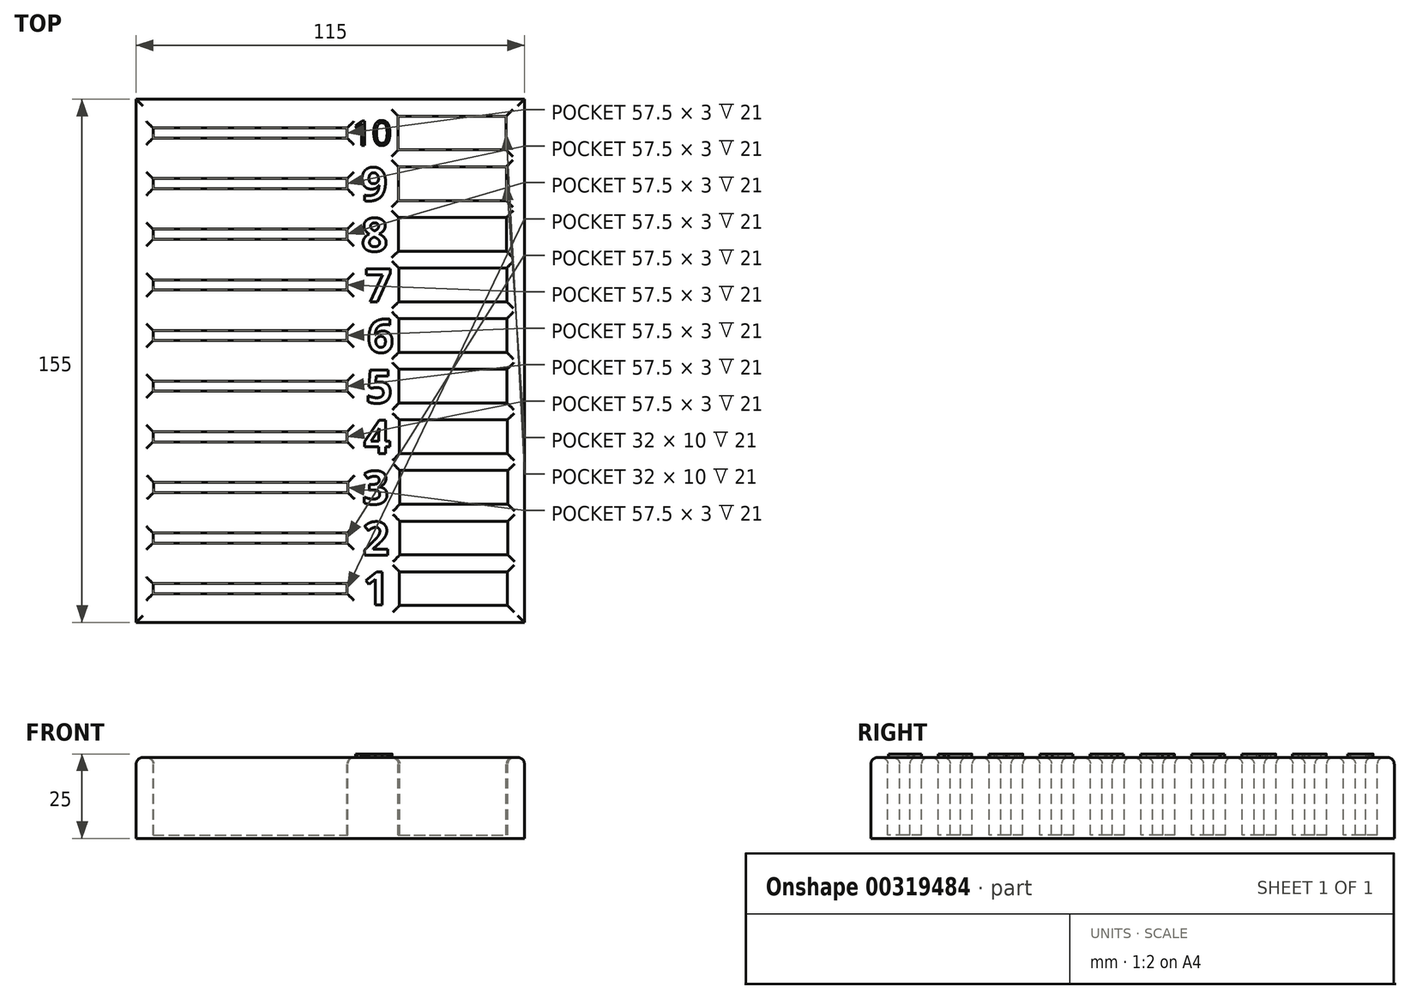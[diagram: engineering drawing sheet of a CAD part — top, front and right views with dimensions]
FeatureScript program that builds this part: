
annotation { "Feature Type Name" : "Feature", "Feature Type Description" : "" }
export const myFeature = defineFeature(function(context is Context, id is Id, definition is map)
    precondition{}
    {
        {
            var Q0;
            Q0=qCreatedBy(makeId("Top.planeOp"),FACE);
            var sketch = newSketch(context, id + "F0", { "sketchPlane" : qUnion([Q0])});
            skLineSegment(sketch, "E0.bottom", {"start": v(-49.85, 126.63) * mm, "end": v(65.15, 126.63) * mm});
            skLineSegment(sketch, "E0.top", {"start": v(-49.85, -28.37) * mm, "end": v(65.15, -28.37) * mm});
            skLineSegment(sketch, "E0.left", {"start": v(-49.85, 126.63) * mm, "end": v(-49.85, -28.37) * mm});
            skLineSegment(sketch, "E0.right", {"start": v(65.15, 126.63) * mm, "end": v(65.15, -28.37) * mm});
            skSolve(sketch);
        }
        {
            var Q0;
            Q0=makeQuery(id+"F0.imprint","IMPRINT",FACE,{"disambiguationData":[TD([[makeQuery(id+"F0.imprint","IMPRINT",EDGE,{"derivedFrom":sQuery(id+"F0.wireOp",EDGE,"E0.bottom")}),-1.0]])]});
            var Q1;
            Q1=makeQuery(id+"F0.imprint","IMPRINT",FACE,{"disambiguationData":[TD([[makeQuery(id+"F0.imprint","IMPRINT",EDGE,{"derivedFrom":sQuery(id+"F0.wireOp",EDGE,"eXpO4zti-W6eb-gkUP-Bc0d-zbJJjk6ygzeg.bottom")}),-1.0]])]});
            var Q2;
            Q2=makeQuery(id+"F0.imprint","IMPRINT",FACE,{"disambiguationData":[TD([[makeQuery(id+"F0.imprint","IMPRINT",EDGE,{"derivedFrom":sQuery(id+"F0.wireOp",EDGE,"IiJkesfC-iyIp-GpGT-9vFS-BzQ84R5pHUzr.bottom")}),-1.0]])]});
            extrude(context, id + "F1", {"entities" : qUnion([Q0, Q1, Q2]), "depth" : 24 * mm});
        }
        {
            var Q0;
            Q0=makeQuery(id+"F1.opExtrude","CAP_FACE",FACE,{"disambiguationData":[OSD([sQuery(id+"F0.wireOp",EDGE,"E0.bottom"),sQuery(id+"F0.wireOp",EDGE,"E0.top"),sQuery(id+"F0.wireOp",EDGE,"E0.left"),sQuery(id+"F0.wireOp",EDGE,"E0.right")])],"isStart":false});
            var sketch = newSketch(context, id + "F2", { "sketchPlane" : qUnion([Q0])});
            skLineSegment(sketch, "E1.bottom", {"start": v(-44.85, -16.87) * mm, "end": v(12.65, -16.87) * mm});
            skLineSegment(sketch, "E1.top", {"start": v(-44.85, -19.87) * mm, "end": v(12.65, -19.87) * mm});
            skLineSegment(sketch, "E1.left", {"start": v(-44.85, -16.87) * mm, "end": v(-44.85, -19.87) * mm});
            skLineSegment(sketch, "E1.right", {"start": v(12.65, -16.87) * mm, "end": v(12.65, -19.87) * mm});
            skLineSegment(sketch, "E2.bottom", {"start": v(28.15, -13.37) * mm, "end": v(60.15, -13.37) * mm});
            skLineSegment(sketch, "E2.top", {"start": v(28.15, -23.37) * mm, "end": v(60.15, -23.37) * mm});
            skLineSegment(sketch, "E2.left", {"start": v(28.15, -13.37) * mm, "end": v(28.15, -23.37) * mm});
            skLineSegment(sketch, "E2.right", {"start": v(60.15, -13.37) * mm, "end": v(60.15, -23.37) * mm});
            skText(sketch, "E3", { "text": "1", "fontName": "OpenSans-Bold.ttf"});
            skLineSegment(sketch, "E4.bottom", {"start": v(-44.87, -1.87) * mm, "end": v(12.63, -1.87) * mm});
            skLineSegment(sketch, "E4.top", {"start": v(-44.87, -4.87) * mm, "end": v(12.63, -4.87) * mm});
            skLineSegment(sketch, "E4.left", {"start": v(-44.87, -1.87) * mm, "end": v(-44.87, -4.87) * mm});
            skLineSegment(sketch, "E4.right", {"start": v(12.63, -1.87) * mm, "end": v(12.63, -4.87) * mm});
            skLineSegment(sketch, "E5.bottom", {"start": v(28.23, 1.63) * mm, "end": v(60.23, 1.63) * mm});
            skLineSegment(sketch, "E5.top", {"start": v(28.23, -8.37) * mm, "end": v(60.23, -8.37) * mm});
            skLineSegment(sketch, "E5.left", {"start": v(28.23, 1.63) * mm, "end": v(28.23, -8.37) * mm});
            skLineSegment(sketch, "E5.right", {"start": v(60.23, 1.63) * mm, "end": v(60.23, -8.37) * mm});
            skLineSegment(sketch, "E6.bottom", {"start": v(28.24, 16.63) * mm, "end": v(60.24, 16.63) * mm});
            skLineSegment(sketch, "E6.top", {"start": v(28.24, 6.63) * mm, "end": v(60.24, 6.63) * mm});
            skLineSegment(sketch, "E6.left", {"start": v(28.24, 16.63) * mm, "end": v(28.24, 6.63) * mm});
            skLineSegment(sketch, "E6.right", {"start": v(60.24, 16.63) * mm, "end": v(60.24, 6.63) * mm});
            skLineSegment(sketch, "E7.bottom", {"start": v(28.1, 31.63) * mm, "end": v(60.1, 31.63) * mm});
            skLineSegment(sketch, "E7.top", {"start": v(28.1, 21.63) * mm, "end": v(60.1, 21.63) * mm});
            skLineSegment(sketch, "E7.left", {"start": v(28.1, 31.63) * mm, "end": v(28.1, 21.63) * mm});
            skLineSegment(sketch, "E7.right", {"start": v(60.1, 31.63) * mm, "end": v(60.1, 21.63) * mm});
            skLineSegment(sketch, "E8.bottom", {"start": v(28, 46.63) * mm, "end": v(60, 46.63) * mm});
            skLineSegment(sketch, "E8.top", {"start": v(28, 36.63) * mm, "end": v(60, 36.63) * mm});
            skLineSegment(sketch, "E8.left", {"start": v(28, 46.63) * mm, "end": v(28, 36.63) * mm});
            skLineSegment(sketch, "E8.right", {"start": v(60, 46.63) * mm, "end": v(60, 36.63) * mm});
            skLineSegment(sketch, "E9.bottom", {"start": v(27.93, 61.63) * mm, "end": v(59.93, 61.63) * mm});
            skLineSegment(sketch, "E9.top", {"start": v(27.93, 51.63) * mm, "end": v(59.93, 51.63) * mm});
            skLineSegment(sketch, "E9.left", {"start": v(27.93, 61.63) * mm, "end": v(27.93, 51.63) * mm});
            skLineSegment(sketch, "E9.right", {"start": v(59.93, 61.63) * mm, "end": v(59.93, 51.63) * mm});
            skLineSegment(sketch, "E10.bottom", {"start": v(27.91, 76.63) * mm, "end": v(59.91, 76.63) * mm});
            skLineSegment(sketch, "E10.top", {"start": v(27.91, 66.63) * mm, "end": v(59.91, 66.63) * mm});
            skLineSegment(sketch, "E10.left", {"start": v(27.91, 76.63) * mm, "end": v(27.91, 66.63) * mm});
            skLineSegment(sketch, "E10.right", {"start": v(59.91, 76.63) * mm, "end": v(59.91, 66.63) * mm});
            skLineSegment(sketch, "E11.bottom", {"start": v(27.82, 91.63) * mm, "end": v(59.82, 91.63) * mm});
            skLineSegment(sketch, "E11.top", {"start": v(27.82, 81.63) * mm, "end": v(59.82, 81.63) * mm});
            skLineSegment(sketch, "E11.left", {"start": v(27.82, 91.63) * mm, "end": v(27.82, 81.63) * mm});
            skLineSegment(sketch, "E11.right", {"start": v(59.82, 91.63) * mm, "end": v(59.82, 81.63) * mm});
            skLineSegment(sketch, "E12.bottom", {"start": v(27.78, 106.63) * mm, "end": v(59.78, 106.63) * mm});
            skLineSegment(sketch, "E12.top", {"start": v(27.78, 96.63) * mm, "end": v(59.78, 96.63) * mm});
            skLineSegment(sketch, "E12.left", {"start": v(27.78, 106.63) * mm, "end": v(27.78, 96.63) * mm});
            skLineSegment(sketch, "E12.right", {"start": v(59.78, 106.63) * mm, "end": v(59.78, 96.63) * mm});
            skLineSegment(sketch, "E13.bottom", {"start": v(27.76, 121.63) * mm, "end": v(59.76, 121.63) * mm});
            skLineSegment(sketch, "E13.top", {"start": v(27.76, 111.63) * mm, "end": v(59.76, 111.63) * mm});
            skLineSegment(sketch, "E13.left", {"start": v(27.76, 121.63) * mm, "end": v(27.76, 111.63) * mm});
            skLineSegment(sketch, "E13.right", {"start": v(59.76, 121.63) * mm, "end": v(59.76, 111.63) * mm});
            skLineSegment(sketch, "E14.bottom", {"start": v(-44.66, 13.13) * mm, "end": v(12.84, 13.13) * mm});
            skLineSegment(sketch, "E14.top", {"start": v(-44.66, 10.13) * mm, "end": v(12.84, 10.13) * mm});
            skLineSegment(sketch, "E14.left", {"start": v(-44.66, 13.13) * mm, "end": v(-44.66, 10.13) * mm});
            skLineSegment(sketch, "E14.right", {"start": v(12.84, 13.13) * mm, "end": v(12.84, 10.13) * mm});
            skLineSegment(sketch, "E15.bottom", {"start": v(-44.85, 28.13) * mm, "end": v(12.65, 28.13) * mm});
            skLineSegment(sketch, "E15.top", {"start": v(-44.85, 25.13) * mm, "end": v(12.65, 25.13) * mm});
            skLineSegment(sketch, "E15.left", {"start": v(-44.85, 28.13) * mm, "end": v(-44.85, 25.13) * mm});
            skLineSegment(sketch, "E15.right", {"start": v(12.65, 28.13) * mm, "end": v(12.65, 25.13) * mm});
            skLineSegment(sketch, "E16.bottom", {"start": v(-44.85, 43.13) * mm, "end": v(12.65, 43.13) * mm});
            skLineSegment(sketch, "E16.top", {"start": v(-44.85, 40.13) * mm, "end": v(12.65, 40.13) * mm});
            skLineSegment(sketch, "E16.left", {"start": v(-44.85, 43.13) * mm, "end": v(-44.85, 40.13) * mm});
            skLineSegment(sketch, "E16.right", {"start": v(12.65, 43.13) * mm, "end": v(12.65, 40.13) * mm});
            skLineSegment(sketch, "E17.bottom", {"start": v(-44.85, 58.13) * mm, "end": v(12.65, 58.13) * mm});
            skLineSegment(sketch, "E17.top", {"start": v(-44.85, 55.13) * mm, "end": v(12.65, 55.13) * mm});
            skLineSegment(sketch, "E17.left", {"start": v(-44.85, 58.13) * mm, "end": v(-44.85, 55.13) * mm});
            skLineSegment(sketch, "E17.right", {"start": v(12.65, 58.13) * mm, "end": v(12.65, 55.13) * mm});
            skLineSegment(sketch, "E18.bottom", {"start": v(-44.85, 73.13) * mm, "end": v(12.65, 73.13) * mm});
            skLineSegment(sketch, "E18.top", {"start": v(-44.85, 70.13) * mm, "end": v(12.65, 70.13) * mm});
            skLineSegment(sketch, "E18.left", {"start": v(-44.85, 73.13) * mm, "end": v(-44.85, 70.13) * mm});
            skLineSegment(sketch, "E18.right", {"start": v(12.65, 73.13) * mm, "end": v(12.65, 70.13) * mm});
            skLineSegment(sketch, "E19.bottom", {"start": v(-44.85, 88.13) * mm, "end": v(12.65, 88.13) * mm});
            skLineSegment(sketch, "E19.top", {"start": v(-44.85, 85.13) * mm, "end": v(12.65, 85.13) * mm});
            skLineSegment(sketch, "E19.left", {"start": v(-44.85, 88.13) * mm, "end": v(-44.85, 85.13) * mm});
            skLineSegment(sketch, "E19.right", {"start": v(12.65, 88.13) * mm, "end": v(12.65, 85.13) * mm});
            skLineSegment(sketch, "E20.bottom", {"start": v(-44.85, 103.13) * mm, "end": v(12.65, 103.13) * mm});
            skLineSegment(sketch, "E20.top", {"start": v(-44.85, 100.13) * mm, "end": v(12.65, 100.13) * mm});
            skLineSegment(sketch, "E20.left", {"start": v(-44.85, 103.13) * mm, "end": v(-44.85, 100.13) * mm});
            skLineSegment(sketch, "E20.right", {"start": v(12.65, 103.13) * mm, "end": v(12.65, 100.13) * mm});
            skLineSegment(sketch, "E21.bottom", {"start": v(-44.85, 118.13) * mm, "end": v(12.65, 118.13) * mm});
            skLineSegment(sketch, "E21.top", {"start": v(-44.85, 115.13) * mm, "end": v(12.65, 115.13) * mm});
            skLineSegment(sketch, "E21.left", {"start": v(-44.85, 118.13) * mm, "end": v(-44.85, 115.13) * mm});
            skLineSegment(sketch, "E21.right", {"start": v(12.65, 118.13) * mm, "end": v(12.65, 115.13) * mm});
            skText(sketch, "E22", { "text": "2", "fontName": "OpenSans-Bold.ttf"});
            skText(sketch, "E23", { "text": "3", "fontName": "OpenSans-Bold.ttf"});
            skText(sketch, "E24", { "text": "4", "fontName": "OpenSans-Bold.ttf"});
            skText(sketch, "E25", { "text": "5", "fontName": "OpenSans-Bold.ttf"});
            skText(sketch, "E26", { "text": "6", "fontName": "OpenSans-Bold.ttf"});
            skText(sketch, "E27", { "text": "7", "fontName": "OpenSans-Bold.ttf"});
            skText(sketch, "E28", { "text": "8", "fontName": "OpenSans-Bold.ttf"});
            skText(sketch, "E29", { "text": "9", "fontName": "OpenSans-Bold.ttf"});
            skText(sketch, "E30", { "text": "10", "fontName": "OpenSans-Regular.ttf"});
            const initialGuessF2  = {"E3": [0.01732, -0.0232, 1, 0, 0.0099], "E22": [0.01725, -0.00843, 1, 0, 0.0099], "E23": [0.01713, 0.00666, 1, 0, 0.0099], "E24": [0.01761, 0.02167, 1, 0, 0.0099], "E25": [0.01821, 0.03663, 1, 0, 0.0099], "E26": [0.01857, 0.0516, 1, 0, 0.0099], "E27": [0.01797, 0.0666, 1, 0, 0.0099], "E28": [0.01684, 0.08158, 1, 0, 0.0099], "E29": [0.01664, 0.0966, 1, 0, 0.0099], "E30": [0.0142, 0.113, 1, 0, 0.00732]};
            skSetInitialGuess(sketch, initialGuessF2);
            skSolve(sketch);
        }
        {
            var Q0;
            Q0=makeQuery(id+"F2.imprint","IMPRINT",FACE,{"disambiguationData":[TD([[makeQuery(id+"F2.imprint","IMPRINT",EDGE,{"derivedFrom":sQuery(id+"F2.wireOp",EDGE,"E2.bottom")}),-1.0]])]});
            var Q1;
            Q1=makeQuery(id+"F2.imprint","IMPRINT",FACE,{"disambiguationData":[TD([[makeQuery(id+"F2.imprint","IMPRINT",EDGE,{"derivedFrom":sQuery(id+"F2.wireOp",EDGE,"E1.bottom")}),-1.0]])]});
            var Q2;
            Q2=makeQuery(id+"F2.imprint","IMPRINT",FACE,{"disambiguationData":[TD([[makeQuery(id+"F2.imprint","IMPRINT",EDGE,{"derivedFrom":sQuery(id+"F2.wireOp",EDGE,"E4.bottom")}),-1.0]])]});
            var Q3;
            Q3=makeQuery(id+"F2.imprint","IMPRINT",FACE,{"disambiguationData":[TD([[makeQuery(id+"F2.imprint","IMPRINT",EDGE,{"derivedFrom":sQuery(id+"F2.wireOp",EDGE,"E5.bottom")}),-1.0]])]});
            var Q4;
            Q4=makeQuery(id+"F2.imprint","IMPRINT",FACE,{"disambiguationData":[TD([[makeQuery(id+"F2.imprint","IMPRINT",EDGE,{"derivedFrom":sQuery(id+"F2.wireOp",EDGE,"E6.bottom")}),-1.0]])]});
            var Q5;
            Q5=makeQuery(id+"F2.imprint","IMPRINT",FACE,{"disambiguationData":[TD([[makeQuery(id+"F2.imprint","IMPRINT",EDGE,{"derivedFrom":sQuery(id+"F2.wireOp",EDGE,"E7.bottom")}),-1.0]])]});
            var Q6;
            Q6=makeQuery(id+"F2.imprint","IMPRINT",FACE,{"disambiguationData":[TD([[makeQuery(id+"F2.imprint","IMPRINT",EDGE,{"derivedFrom":sQuery(id+"F2.wireOp",EDGE,"E8.bottom")}),-1.0]])]});
            var Q7;
            Q7=makeQuery(id+"F2.imprint","IMPRINT",FACE,{"disambiguationData":[TD([[makeQuery(id+"F2.imprint","IMPRINT",EDGE,{"derivedFrom":sQuery(id+"F2.wireOp",EDGE,"E9.bottom")}),-1.0]])]});
            var Q8;
            Q8=makeQuery(id+"F2.imprint","IMPRINT",FACE,{"disambiguationData":[TD([[makeQuery(id+"F2.imprint","IMPRINT",EDGE,{"derivedFrom":sQuery(id+"F2.wireOp",EDGE,"E10.bottom")}),-1.0]])]});
            var Q9;
            Q9=makeQuery(id+"F2.imprint","IMPRINT",FACE,{"disambiguationData":[TD([[makeQuery(id+"F2.imprint","IMPRINT",EDGE,{"derivedFrom":sQuery(id+"F2.wireOp",EDGE,"E11.bottom")}),-1.0]])]});
            var Q10;
            Q10=makeQuery(id+"F2.imprint","IMPRINT",FACE,{"disambiguationData":[TD([[makeQuery(id+"F2.imprint","IMPRINT",EDGE,{"derivedFrom":sQuery(id+"F2.wireOp",EDGE,"E12.bottom")}),-1.0]])]});
            var Q11;
            Q11=makeQuery(id+"F2.imprint","IMPRINT",FACE,{"disambiguationData":[TD([[makeQuery(id+"F2.imprint","IMPRINT",EDGE,{"derivedFrom":sQuery(id+"F2.wireOp",EDGE,"E13.bottom")}),-1.0]])]});
            var Q12;
            Q12=makeQuery(id+"F2.imprint","IMPRINT",FACE,{"disambiguationData":[TD([[makeQuery(id+"F2.imprint","IMPRINT",EDGE,{"derivedFrom":sQuery(id+"F2.wireOp",EDGE,"E14.bottom")}),-1.0]])]});
            var Q13;
            Q13=makeQuery(id+"F2.imprint","IMPRINT",FACE,{"disambiguationData":[TD([[makeQuery(id+"F2.imprint","IMPRINT",EDGE,{"derivedFrom":sQuery(id+"F2.wireOp",EDGE,"E15.bottom")}),-1.0]])]});
            var Q14;
            Q14=makeQuery(id+"F2.imprint","IMPRINT",FACE,{"disambiguationData":[TD([[makeQuery(id+"F2.imprint","IMPRINT",EDGE,{"derivedFrom":sQuery(id+"F2.wireOp",EDGE,"E16.bottom")}),-1.0]])]});
            var Q15;
            Q15=makeQuery(id+"F2.imprint","IMPRINT",FACE,{"disambiguationData":[TD([[makeQuery(id+"F2.imprint","IMPRINT",EDGE,{"derivedFrom":sQuery(id+"F2.wireOp",EDGE,"E17.bottom")}),-1.0]])]});
            var Q16;
            Q16=makeQuery(id+"F2.imprint","IMPRINT",FACE,{"disambiguationData":[TD([[makeQuery(id+"F2.imprint","IMPRINT",EDGE,{"derivedFrom":sQuery(id+"F2.wireOp",EDGE,"E18.bottom")}),-1.0]])]});
            var Q17;
            Q17=makeQuery(id+"F2.imprint","IMPRINT",FACE,{"disambiguationData":[TD([[makeQuery(id+"F2.imprint","IMPRINT",EDGE,{"derivedFrom":sQuery(id+"F2.wireOp",EDGE,"E19.bottom")}),-1.0]])]});
            var Q18;
            Q18=makeQuery(id+"F2.imprint","IMPRINT",FACE,{"disambiguationData":[TD([[makeQuery(id+"F2.imprint","IMPRINT",EDGE,{"derivedFrom":sQuery(id+"F2.wireOp",EDGE,"E20.bottom")}),-1.0]])]});
            var Q19;
            Q19=makeQuery(id+"F2.imprint","IMPRINT",FACE,{"disambiguationData":[TD([[makeQuery(id+"F2.imprint","IMPRINT",EDGE,{"derivedFrom":sQuery(id+"F2.wireOp",EDGE,"E21.bottom")}),-1.0]])]});
            extrude(context, id + "F3", {"entities" : qUnion([Q0, Q1, Q2, Q3, Q4, Q5, Q6, Q7, Q8, Q9, Q10, Q11, Q12, Q13, Q14, Q15, Q16, Q17, Q18, Q19]), "operationType" : NewBodyOperationType.REMOVE, "oppositeDirection" : true, "depth" : 23 * mm});
        }
        {
            var Q0;
            Q0=makeQuery(id+"F3.boolean.opBoolean","COPY",EDGE,{"derivedFrom":makeQuery(id+"F3.opExtrude","CAP_EDGE",EDGE,{"disambiguationData":[OSD([sQuery(id+"F2.wireOp",EDGE,"E1.top")])],"isStart":true})});
            var Q1;
            Q1=makeQuery(id+"F3.boolean.opBoolean","COPY",EDGE,{"derivedFrom":makeQuery(id+"F3.opExtrude","CAP_EDGE",EDGE,{"disambiguationData":[OSD([sQuery(id+"F2.wireOp",EDGE,"E1.bottom")])],"isStart":true})});
            var Q2;
            Q2=makeQuery(id+"F3.boolean.opBoolean","COPY",EDGE,{"derivedFrom":makeQuery(id+"F3.opExtrude","CAP_EDGE",EDGE,{"disambiguationData":[OSD([sQuery(id+"F2.wireOp",EDGE,"E1.right")])],"isStart":true})});
            var Q3;
            Q3=makeQuery(id+"F3.boolean.opBoolean","COPY",EDGE,{"derivedFrom":makeQuery(id+"F3.opExtrude","CAP_EDGE",EDGE,{"disambiguationData":[OSD([sQuery(id+"F2.wireOp",EDGE,"E1.left")])],"isStart":true})});
            var Q4;
            Q4=makeQuery(id+"F3.boolean.opBoolean","COPY",EDGE,{"derivedFrom":makeQuery(id+"F3.opExtrude","CAP_EDGE",EDGE,{"disambiguationData":[OSD([sQuery(id+"F2.wireOp",EDGE,"E2.bottom")])],"isStart":true})});
            var Q5;
            Q5=makeQuery(id+"F3.boolean.opBoolean","COPY",EDGE,{"derivedFrom":makeQuery(id+"F3.opExtrude","CAP_EDGE",EDGE,{"disambiguationData":[OSD([sQuery(id+"F2.wireOp",EDGE,"E2.top")])],"isStart":true})});
            var Q6;
            Q6=makeQuery(id+"F3.boolean.opBoolean","COPY",EDGE,{"derivedFrom":makeQuery(id+"F3.opExtrude","CAP_EDGE",EDGE,{"disambiguationData":[OSD([sQuery(id+"F2.wireOp",EDGE,"E2.left")])],"isStart":true})});
            var Q7;
            Q7=makeQuery(id+"F3.boolean.opBoolean","COPY",EDGE,{"derivedFrom":makeQuery(id+"F3.opExtrude","CAP_EDGE",EDGE,{"disambiguationData":[OSD([sQuery(id+"F2.wireOp",EDGE,"E2.right")])],"isStart":true})});
            var Q8;
            Q8=makeQuery(id+"F3.boolean.opBoolean","COPY",EDGE,{"derivedFrom":makeQuery(id+"F3.opExtrude","CAP_EDGE",EDGE,{"disambiguationData":[OSD([sQuery(id+"F2.wireOp",EDGE,"E4.bottom")])],"isStart":true})});
            var Q9;
            Q9=makeQuery(id+"F3.boolean.opBoolean","COPY",EDGE,{"derivedFrom":makeQuery(id+"F3.opExtrude","CAP_EDGE",EDGE,{"disambiguationData":[OSD([sQuery(id+"F2.wireOp",EDGE,"E4.top")])],"isStart":true})});
            var Q10;
            Q10=makeQuery(id+"F3.boolean.opBoolean","COPY",EDGE,{"derivedFrom":makeQuery(id+"F3.opExtrude","CAP_EDGE",EDGE,{"disambiguationData":[OSD([sQuery(id+"F2.wireOp",EDGE,"E4.left")])],"isStart":true})});
            var Q11;
            Q11=makeQuery(id+"F3.boolean.opBoolean","COPY",EDGE,{"derivedFrom":makeQuery(id+"F3.opExtrude","CAP_EDGE",EDGE,{"disambiguationData":[OSD([sQuery(id+"F2.wireOp",EDGE,"E4.right")])],"isStart":true})});
            var Q12;
            Q12=makeQuery(id+"F3.boolean.opBoolean","COPY",EDGE,{"derivedFrom":makeQuery(id+"F3.opExtrude","CAP_EDGE",EDGE,{"disambiguationData":[OSD([sQuery(id+"F2.wireOp",EDGE,"E5.left")])],"isStart":true})});
            var Q13;
            Q13=makeQuery(id+"F3.boolean.opBoolean","COPY",EDGE,{"derivedFrom":makeQuery(id+"F3.opExtrude","CAP_EDGE",EDGE,{"disambiguationData":[OSD([sQuery(id+"F2.wireOp",EDGE,"E5.bottom")])],"isStart":true})});
            var Q14;
            Q14=makeQuery(id+"F3.boolean.opBoolean","COPY",EDGE,{"derivedFrom":makeQuery(id+"F3.opExtrude","CAP_EDGE",EDGE,{"disambiguationData":[OSD([sQuery(id+"F2.wireOp",EDGE,"E5.right")])],"isStart":true})});
            var Q15;
            Q15=makeQuery(id+"F3.boolean.opBoolean","COPY",EDGE,{"derivedFrom":makeQuery(id+"F3.opExtrude","CAP_EDGE",EDGE,{"disambiguationData":[OSD([sQuery(id+"F2.wireOp",EDGE,"E5.top")])],"isStart":true})});
            var Q16;
            Q16=makeQuery(id+"F3.boolean.opBoolean","COPY",EDGE,{"derivedFrom":makeQuery(id+"F3.opExtrude","CAP_EDGE",EDGE,{"disambiguationData":[OSD([sQuery(id+"F2.wireOp",EDGE,"E6.top")])],"isStart":true})});
            var Q17;
            Q17=makeQuery(id+"F3.boolean.opBoolean","COPY",EDGE,{"derivedFrom":makeQuery(id+"F3.opExtrude","CAP_EDGE",EDGE,{"disambiguationData":[OSD([sQuery(id+"F2.wireOp",EDGE,"E6.left")])],"isStart":true})});
            var Q18;
            Q18=makeQuery(id+"F3.boolean.opBoolean","COPY",EDGE,{"derivedFrom":makeQuery(id+"F3.opExtrude","CAP_EDGE",EDGE,{"disambiguationData":[OSD([sQuery(id+"F2.wireOp",EDGE,"E6.bottom")])],"isStart":true})});
            var Q19;
            Q19=makeQuery(id+"F3.boolean.opBoolean","COPY",EDGE,{"derivedFrom":makeQuery(id+"F3.opExtrude","CAP_EDGE",EDGE,{"disambiguationData":[OSD([sQuery(id+"F2.wireOp",EDGE,"E6.right")])],"isStart":true})});
            var Q20;
            Q20=makeQuery(id+"F3.boolean.opBoolean","COPY",EDGE,{"derivedFrom":makeQuery(id+"F3.opExtrude","CAP_EDGE",EDGE,{"disambiguationData":[OSD([sQuery(id+"F2.wireOp",EDGE,"E7.top")])],"isStart":true})});
            var Q21;
            Q21=makeQuery(id+"F3.boolean.opBoolean","COPY",EDGE,{"derivedFrom":makeQuery(id+"F3.opExtrude","CAP_EDGE",EDGE,{"disambiguationData":[OSD([sQuery(id+"F2.wireOp",EDGE,"E7.right")])],"isStart":true})});
            var Q22;
            Q22=makeQuery(id+"F3.boolean.opBoolean","COPY",EDGE,{"derivedFrom":makeQuery(id+"F3.opExtrude","CAP_EDGE",EDGE,{"disambiguationData":[OSD([sQuery(id+"F2.wireOp",EDGE,"E7.bottom")])],"isStart":true})});
            var Q23;
            Q23=makeQuery(id+"F3.boolean.opBoolean","COPY",EDGE,{"derivedFrom":makeQuery(id+"F3.opExtrude","CAP_EDGE",EDGE,{"disambiguationData":[OSD([sQuery(id+"F2.wireOp",EDGE,"E7.left")])],"isStart":true})});
            var Q24;
            Q24=makeQuery(id+"F3.boolean.opBoolean","COPY",EDGE,{"derivedFrom":makeQuery(id+"F3.opExtrude","CAP_EDGE",EDGE,{"disambiguationData":[OSD([sQuery(id+"F2.wireOp",EDGE,"E8.left")])],"isStart":true})});
            var Q25;
            Q25=makeQuery(id+"F3.boolean.opBoolean","COPY",EDGE,{"derivedFrom":makeQuery(id+"F3.opExtrude","CAP_EDGE",EDGE,{"disambiguationData":[OSD([sQuery(id+"F2.wireOp",EDGE,"E8.bottom")])],"isStart":true})});
            var Q26;
            Q26=makeQuery(id+"F1.opExtrude","CAP_FACE",FACE,{"disambiguationData":[OSD([sQuery(id+"F0.wireOp",EDGE,"E0.bottom"),sQuery(id+"F0.wireOp",EDGE,"E0.top"),sQuery(id+"F0.wireOp",EDGE,"E0.left"),sQuery(id+"F0.wireOp",EDGE,"E0.right")])],"isStart":false});
            var Q27;
            Q27=makeQuery(id+"F3.boolean.opBoolean","COPY",EDGE,{"derivedFrom":makeQuery(id+"F3.opExtrude","CAP_EDGE",EDGE,{"disambiguationData":[OSD([sQuery(id+"F2.wireOp",EDGE,"E8.right")])],"isStart":true})});
            fillet(context, id + "F4", {"entities" : qUnion([Q0, Q1, Q2, Q3, Q4, Q5, Q6, Q7, Q8, Q9, Q10, Q11, Q12, Q13, Q14, Q15, Q16, Q17, Q18, Q19, Q20, Q21, Q22, Q23, Q24, Q25, Q26, Q27]), "radius" : 2 * mm, "tangentPropagation" : true, "allowEdgeOverflow" : false});
        }
        {
            var Q0;
            Q0=makeQuery(id+"F2.imprint","IMPRINT",FACE,{"disambiguationData":[TD([[makeQuery(id+"F2.imprint","IMPRINT",EDGE,{"derivedFrom":sQuery(id+"F2.wireOp",EDGE,"E3.sketch_text.stroke-0")}),-1.0]])]});
            var Q1;
            Q1=makeQuery(id+"F2.imprint","IMPRINT",FACE,{"disambiguationData":[TD([[makeQuery(id+"F2.imprint","IMPRINT",EDGE,{"derivedFrom":sQuery(id+"F2.wireOp",EDGE,"E22.sketch_text.stroke-0")}),-1.0]])]});
            var Q2;
            Q2=makeQuery(id+"F2.imprint","IMPRINT",FACE,{"disambiguationData":[TD([[makeQuery(id+"F2.imprint","IMPRINT",EDGE,{"derivedFrom":sQuery(id+"F2.wireOp",EDGE,"E23.sketch_text.stroke-0")}),-1.0]])]});
            var Q3;
            Q3=makeQuery(id+"F2.imprint","IMPRINT",FACE,{"disambiguationData":[TD([[makeQuery(id+"F2.imprint","IMPRINT",EDGE,{"derivedFrom":sQuery(id+"F2.wireOp",EDGE,"E24.sketch_text.stroke-0")}),-1.0]])]});
            var Q4;
            Q4=makeQuery(id+"F2.imprint","IMPRINT",FACE,{"disambiguationData":[TD([[makeQuery(id+"F2.imprint","IMPRINT",EDGE,{"derivedFrom":sQuery(id+"F2.wireOp",EDGE,"E25.sketch_text.stroke-0")}),-1.0]])]});
            var Q5;
            Q5=makeQuery(id+"F2.imprint","IMPRINT",FACE,{"disambiguationData":[TD([[makeQuery(id+"F2.imprint","IMPRINT",EDGE,{"derivedFrom":sQuery(id+"F2.wireOp",EDGE,"E26.sketch_text.stroke-0")}),-1.0]])]});
            var Q6;
            Q6=makeQuery(id+"F2.imprint","IMPRINT",FACE,{"disambiguationData":[TD([[makeQuery(id+"F2.imprint","IMPRINT",EDGE,{"derivedFrom":sQuery(id+"F2.wireOp",EDGE,"E27.sketch_text.stroke-0")}),-1.0]])]});
            var Q7;
            Q7=makeQuery(id+"F2.imprint","IMPRINT",FACE,{"disambiguationData":[TD([[makeQuery(id+"F2.imprint","IMPRINT",EDGE,{"derivedFrom":sQuery(id+"F2.wireOp",EDGE,"E28.sketch_text.stroke-0")}),-1.0]])]});
            var Q8;
            Q8=makeQuery(id+"F2.imprint","IMPRINT",FACE,{"disambiguationData":[TD([[makeQuery(id+"F2.imprint","IMPRINT",EDGE,{"derivedFrom":sQuery(id+"F2.wireOp",EDGE,"E29.sketch_text.stroke-0")}),-1.0]])]});
            var Q9;
            Q9=makeQuery(id+"F2.imprint","IMPRINT",FACE,{"disambiguationData":[TD([[makeQuery(id+"F2.imprint","IMPRINT",EDGE,{"derivedFrom":sQuery(id+"F2.wireOp",EDGE,"E30.sketch_text.stroke-0")}),-1.0]])]});
            var Q10;
            Q10=makeQuery(id+"F2.imprint","IMPRINT",FACE,{"disambiguationData":[TD([[makeQuery(id+"F2.imprint","IMPRINT",EDGE,{"derivedFrom":sQuery(id+"F2.wireOp",EDGE,"E30.sketch_text.stroke-9")}),-1.0]])]});
            extrude(context, id + "F5", {"entities" : qUnion([Q0, Q1, Q2, Q3, Q4, Q5, Q6, Q7, Q8, Q9, Q10]), "operationType" : NewBodyOperationType.ADD, "depth" : 1 * mm});
        }
    });
